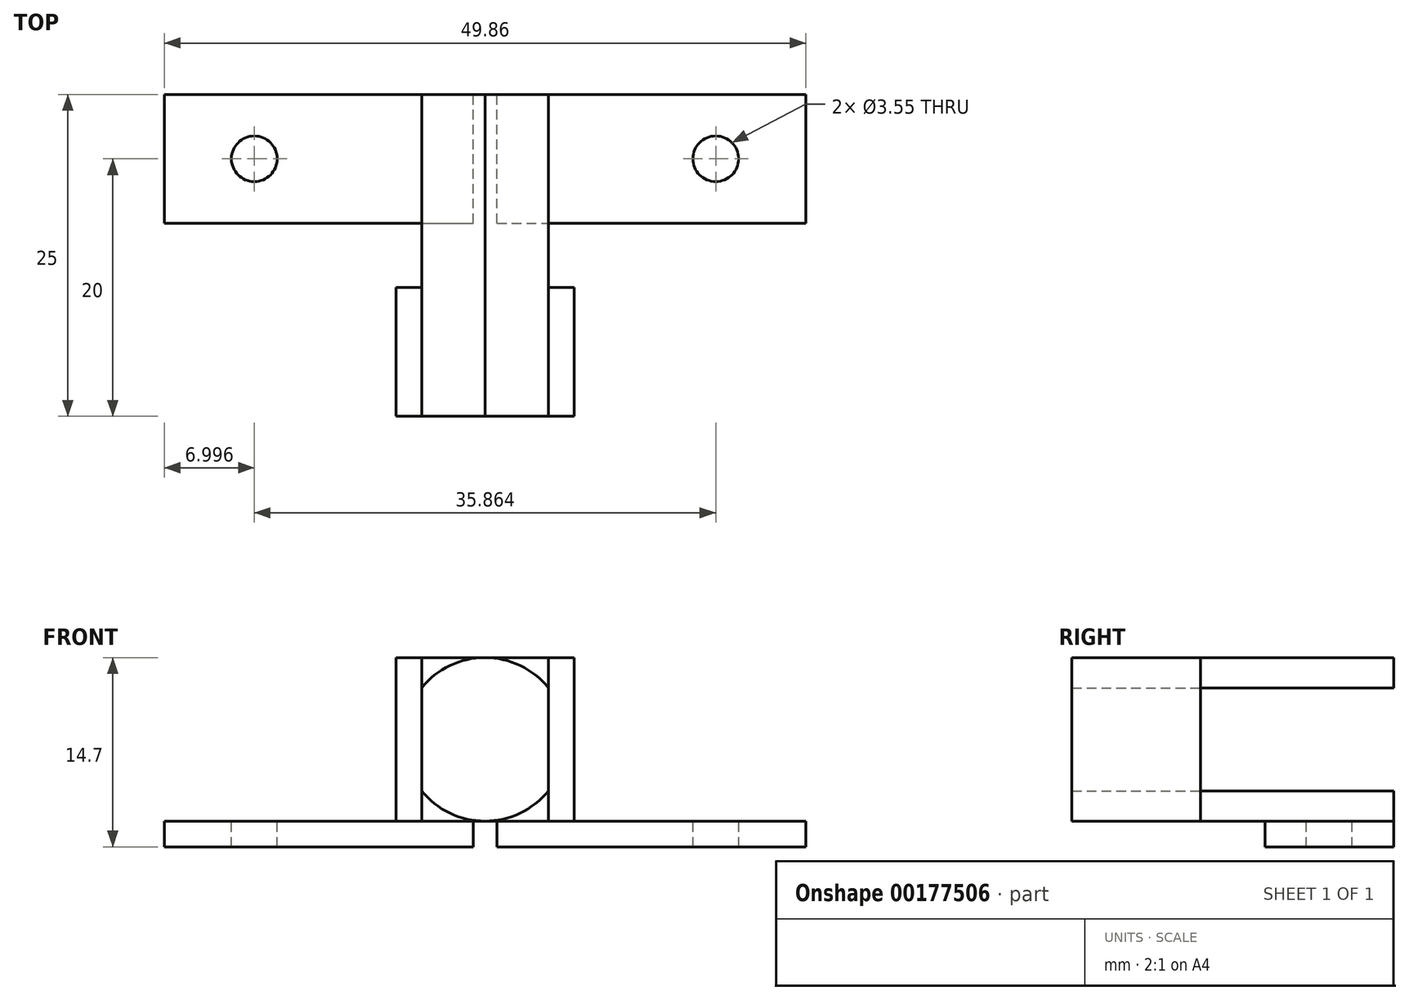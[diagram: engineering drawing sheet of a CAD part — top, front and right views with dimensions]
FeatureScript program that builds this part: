
annotation { "Feature Type Name" : "Feature", "Feature Type Description" : "" }
export const myFeature = defineFeature(function(context is Context, id is Id, definition is map)
    precondition{}
    {
        {
            var Q0;
            Q0=qCreatedBy(makeId("Front.planeOp"),FACE);
            var sketch = newSketch(context, id + "F0", { "sketchPlane" : qUnion([Q0])});
            skArc(sketch, "E0", {"start": v(-9.86, 0) * mm, "mid": v(-4.93, -2.35) * mm, "end": v(0, 0) * mm});
            skArc(sketch, "E1.MirrorCS", {"start": v(-9.86, 8) * mm, "mid": v(-4.93, 10.35) * mm, "end": v(0, 8) * mm});
            skLineSegment(sketch, "E2", {"start": v(-9.86, 8) * mm, "end": v(0, 8) * mm, "construction": true});
            skLineSegment(sketch, "E3", {"start": v(-9.86, 0) * mm, "end": v(0, 0) * mm, "construction": true});
            skLineSegment(sketch, "E4", {"start": v(0, 8) * mm, "end": v(0, 0) * mm, "construction": true});
            skCircle(sketch, "E5", {"center": v(-4.93, 4) * mm, "radius": 6.35 * mm, "construction": true});
            skPoint(sketch, "E6", {"position": v(0, 8) * mm});
            skPoint(sketch, "E7", {"position": v(1.42, 4) * mm});
            skLineSegment(sketch, "E8", {"start": v(-4.93, 4) * mm, "end": v(1.42, 4) * mm, "construction": true});
            skLineSegment(sketch, "E9", {"start": v(-9.86, 8) * mm, "end": v(-9.86, 10.35) * mm});
            skPoint(sketch, "E9.endSnap0", {"position": v(-4.93, 10.35) * mm});
            skLineSegment(sketch, "E10", {"start": v(-9.86, 10.35) * mm, "end": v(-4.93, 10.35) * mm});
            skLineSegment(sketch, "E11", {"start": v(0, 10.35) * mm, "end": v(0, 8) * mm});
            skLineSegment(sketch, "E12", {"start": v(0, 10.35) * mm, "end": v(-4.93, 10.35) * mm});
            skLineSegment(sketch, "E13", {"start": v(-4.93, -2.35) * mm, "end": v(-9.86, -2.35) * mm});
            skLineSegment(sketch, "E14", {"start": v(-9.86, -2.35) * mm, "end": v(-9.86, 0) * mm});
            skLineSegment(sketch, "E15", {"start": v(-4.93, -2.35) * mm, "end": v(0, -2.35) * mm});
            skLineSegment(sketch, "E16", {"start": v(0, -2.35) * mm, "end": v(0, 0) * mm});
            skSolve(sketch);
        }
        {
            var Q0;
            {var subQ0=sQuery(id+"F0.wireOp",EDGE,"E9");Q0=makeQuery(id+"F0.imprint","IMPRINT",FACE,{"disambiguationData":[TD([[makeQuery(id+"F0.imprint","IMPRINT",EDGE,{"derivedFrom":subQ0}),-1.0]])]});}
            var Q1;
            {var subQ0=sQuery(id+"F0.wireOp",EDGE,"E11");Q1=makeQuery(id+"F0.imprint","IMPRINT",FACE,{"disambiguationData":[TD([[makeQuery(id+"F0.imprint","IMPRINT",EDGE,{"derivedFrom":subQ0}),-1.0]])]});}
            var Q2;
            {var subQ2=sQuery(id+"F0.wireOp",EDGE,"E13");Q2=makeQuery(id+"F0.imprint","IMPRINT",FACE,{"disambiguationData":[TD([[makeQuery(id+"F0.imprint","IMPRINT",EDGE,{"derivedFrom":subQ2}),-1.0]])]});}
            var Q3;
            {var subQ2=sQuery(id+"F0.wireOp",EDGE,"E15");Q3=makeQuery(id+"F0.imprint","IMPRINT",FACE,{"disambiguationData":[TD([[makeQuery(id+"F0.imprint","IMPRINT",EDGE,{"derivedFrom":subQ2}),1.0]])]});}
            extrude(context, id + "F1", {"entities" : qUnion([Q0, Q1, Q2, Q3]), "depth" : 25 * mm});
        }
        {
            var Q0;
            Q0=makeQuery(id+"F1.opExtrude","SWEPT_FACE",FACE,{"disambiguationData":[OSD([sQuery(id+"F0.wireOp",EDGE,"E9")])]});
            var sketch = newSketch(context, id + "F2", { "sketchPlane" : qUnion([Q0])});
            skLineSegment(sketch, "E17", {"start": v(15, 10.35) * mm, "end": v(15, -2.35) * mm});
            skPoint(sketch, "E18", {"position": v(15, -2.35) * mm});
            skLineSegment(sketch, "E19", {"start": v(15, 10.35) * mm, "end": v(25, 10.35) * mm});
            skLineSegment(sketch, "E20", {"start": v(25, 10.35) * mm, "end": v(25, -2.35) * mm});
            skPoint(sketch, "E20.endSnap0", {"position": v(25, 9.17) * mm});
            skLineSegment(sketch, "E21", {"start": v(25, -2.35) * mm, "end": v(15, -2.35) * mm});
            skSolve(sketch);
        }
        {
            var Q0;
            {var subQ0=sQuery(id+"F2.wireOp",EDGE,"E21");Q0=makeQuery(id+"F2.imprint","IMPRINT",FACE,{"disambiguationData":[TD([[makeQuery(id+"F2.imprint","IMPRINT",EDGE,{"derivedFrom":subQ0}),-1.0]])]});}
            var Q1;
            {var subQ0=sQuery(id+"F2.wireOp",EDGE,"E19");Q1=makeQuery(id+"F2.imprint","IMPRINT",FACE,{"disambiguationData":[TD([[makeQuery(id+"F2.imprint","IMPRINT",EDGE,{"derivedFrom":subQ0}),1.0]])]});}
            extrude(context, id + "F3", {"entities" : qUnion([Q0, Q1]), "depth" : 2 * mm});
        }
        {
            var Q0;
            Q0=makeQuery(id+"F1.opExtrude","SWEPT_FACE",FACE,{"disambiguationData":[OSD([sQuery(id+"F0.wireOp",EDGE,"E11")])]});
            var sketch = newSketch(context, id + "F4", { "sketchPlane" : qUnion([Q0])});
            skLineSegment(sketch, "E22", {"start": v(-25, 10.35) * mm, "end": v(-25, -2.35) * mm});
            skLineSegment(sketch, "E23", {"start": v(-25, -2.35) * mm, "end": v(-15, -2.35) * mm});
            skLineSegment(sketch, "E24", {"start": v(-15, -2.35) * mm, "end": v(-15, 10.35) * mm});
            skLineSegment(sketch, "E25", {"start": v(-15, 10.35) * mm, "end": v(-25, 10.35) * mm});
            skSolve(sketch);
        }
        {
            var Q0;
            {var subQ4=sQuery(id+"F4.wireOp",EDGE,"E25");Q0=makeQuery(id+"F4.imprint","IMPRINT",FACE,{"disambiguationData":[TD([[makeQuery(id+"F4.imprint","IMPRINT",EDGE,{"derivedFrom":subQ4}),-1.0]])]});}
            var Q1;
            {var subQ3=sQuery(id+"F4.wireOp",EDGE,"E23");Q1=makeQuery(id+"F4.imprint","IMPRINT",FACE,{"disambiguationData":[TD([[makeQuery(id+"F4.imprint","IMPRINT",EDGE,{"derivedFrom":subQ3}),1.0]])]});}
            extrude(context, id + "F5", {"entities" : qUnion([Q0, Q1]), "depth" : 2 * mm});
        }
        {
            var Q0;
            Q0=makeQuery(id+"F1.opExtrude","SWEPT_FACE",FACE,{"disambiguationData":[OSD([sQuery(id+"F0.wireOp",EDGE,"E13")])]});
            var sketch = newSketch(context, id + "F6", { "sketchPlane" : qUnion([Q0])});
            skPoint(sketch, "E26", {"position": v(-9.86, 10) * mm});
            skPoint(sketch, "E27", {"position": v(-5.86, 10) * mm});
            skPoint(sketch, "E28", {"position": v(-5.86, 0) * mm});
            skPoint(sketch, "E29", {"position": v(-9.86, 0) * mm});
            skLineSegment(sketch, "E30", {"start": v(-5.86, 10) * mm, "end": v(-9.86, 10) * mm});
            skLineSegment(sketch, "E31", {"start": v(-5.86, 10) * mm, "end": v(-5.86, 0) * mm});
            skLineSegment(sketch, "E32", {"start": v(-9.86, 0) * mm, "end": v(-29.86, 0) * mm});
            skLineSegment(sketch, "E33", {"start": v(-29.86, 0) * mm, "end": v(-29.86, 10) * mm});
            skLineSegment(sketch, "E34", {"start": v(-29.86, 10) * mm, "end": v(-9.86, 10) * mm});
            skSolve(sketch);
        }
        {
            var Q0;
            {var subQ0=sQuery(id+"F6.wireOp",EDGE,"E32");Q0=makeQuery(id+"F6.imprint","IMPRINT",FACE,{"disambiguationData":[TD([[makeQuery(id+"F6.imprint","IMPRINT",EDGE,{"derivedFrom":subQ0}),-1.0]])]});}
            var Q1;
            {var subQ0=sQuery(id+"F6.wireOp",EDGE,"E30");Q1=makeQuery(id+"F6.imprint","IMPRINT",FACE,{"disambiguationData":[TD([[makeQuery(id+"F6.imprint","IMPRINT",EDGE,{"derivedFrom":subQ0}),1.0]])]});}
            extrude(context, id + "F7", {"entities" : qUnion([Q0, Q1]), "depth" : 2 * mm});
        }
        {
            var Q0;
            Q0=makeQuery(id+"F7.opExtrude","CAP_FACE",FACE,{"disambiguationData":[OSD([sQuery(id+"F0.wireOp",EDGE,"E13"),sQuery(id+"F6.wireOp",EDGE,"E30"),sQuery(id+"F6.wireOp",EDGE,"E31"),sQuery(id+"F6.wireOp",EDGE,"E32"),sQuery(id+"F6.wireOp",EDGE,"E33"),sQuery(id+"F6.wireOp",EDGE,"E34")])],"isStart":true});
            var sketch = newSketch(context, id + "F8", { "sketchPlane" : qUnion([Q0])});
            skLineSegment(sketch, "E35", {"start": v(-29.86, -5) * mm, "end": v(-22.86, -5) * mm});
            skCircle(sketch, "E36", {"center": v(-22.86, -5) * mm, "radius": 1.77 * mm});
            skSolve(sketch);
        }
        {
            var Q0;
            Q0=sQuery(id+"F8.wireOp",VERTEX,"E35.end");
            var Q1;
            Q1=makeQuery(id+"F7.opExtrude","SWEPT_BODY",BODY,{"disambiguationData":[OSD([sQuery(id+"F0.wireOp",EDGE,"E13"),sQuery(id+"F6.wireOp",EDGE,"E30"),sQuery(id+"F6.wireOp",EDGE,"E31"),sQuery(id+"F6.wireOp",EDGE,"E32"),sQuery(id+"F6.wireOp",EDGE,"E33"),sQuery(id+"F6.wireOp",EDGE,"E34")])]});
            hole(context, id + "F9", {"style" : HoleStyle.SIMPLE, "endStyle" : HoleEndStyle.THROUGH, "holeDiameter" : 3.55 * mm, "locations" : qUnion([Q0]), "scope" : qUnion([Q1]), "isTappedThrough" : true});
        }
        {
            var Q0;
            Q0=makeQuery(id+"F1.opExtrude","SWEPT_FACE",FACE,{"disambiguationData":[OSD([sQuery(id+"F0.wireOp",EDGE,"E15")])]});
            var sketch = newSketch(context, id + "F10", { "sketchPlane" : qUnion([Q0])});
            skPoint(sketch, "E37", {"position": v(0, 10) * mm});
            skLineSegment(sketch, "E38", {"start": v(0, 10) * mm, "end": v(-4, 10) * mm});
            skLineSegment(sketch, "E39", {"start": v(0, 0) * mm, "end": v(-4, 0) * mm});
            skLineSegment(sketch, "E40", {"start": v(-4, 10) * mm, "end": v(-4, 0) * mm});
            skLineSegment(sketch, "E41", {"start": v(0, 10) * mm, "end": v(20, 10) * mm});
            skLineSegment(sketch, "E42", {"start": v(0, 0) * mm, "end": v(20, 0) * mm});
            skLineSegment(sketch, "E43", {"start": v(20, 0) * mm, "end": v(20, 10) * mm});
            skSolve(sketch);
        }
        {
            var Q0;
            {var subQ0=sQuery(id+"F10.wireOp",EDGE,"E41");Q0=makeQuery(id+"F10.imprint","IMPRINT",FACE,{"disambiguationData":[TD([[makeQuery(id+"F10.imprint","IMPRINT",EDGE,{"derivedFrom":subQ0}),-1.0]])]});}
            var Q1;
            {var subQ0=sQuery(id+"F10.wireOp",EDGE,"E38");Q1=makeQuery(id+"F10.imprint","IMPRINT",FACE,{"disambiguationData":[TD([[makeQuery(id+"F10.imprint","IMPRINT",EDGE,{"derivedFrom":subQ0}),1.0]])]});}
            extrude(context, id + "F11", {"entities" : qUnion([Q0, Q1]), "operationType" : NewBodyOperationType.ADD, "depth" : 2 * mm});
        }
        {
            var Q0;
            Q0=makeQuery(id+"F11.opExtrude","CAP_FACE",FACE,{"disambiguationData":[OSD([sQuery(id+"F10.wireOp",EDGE,"E38"),sQuery(id+"F10.wireOp",EDGE,"E39"),sQuery(id+"F10.wireOp",EDGE,"E40"),sQuery(id+"F10.wireOp",EDGE,"E41"),sQuery(id+"F10.wireOp",EDGE,"E42"),sQuery(id+"F10.wireOp",EDGE,"E43")])],"isStart":true});
            var sketch = newSketch(context, id + "F12", { "sketchPlane" : qUnion([Q0])});
            skLineSegment(sketch, "E44", {"start": v(20, -5) * mm, "end": v(13, -5) * mm});
            skPoint(sketch, "E44.endSnap0", {"position": v(20, -5) * mm});
            skPoint(sketch, "E45", {"position": v(13, -5) * mm});
            skSolve(sketch);
        }
        {
            var Q0;
            Q0=sQuery(id+"F12.wireOp",VERTEX,"E45");
            var Q1;
            Q1=makeQuery(id+"F1.opExtrude","SWEPT_BODY",BODY,{"disambiguationData":[OSD([sQuery(id+"F0.wireOp",EDGE,"E0"),sQuery(id+"F0.wireOp",EDGE,"E15"),sQuery(id+"F0.wireOp",EDGE,"E16")])]});
            hole(context, id + "F13", {"style" : HoleStyle.SIMPLE, "endStyle" : HoleEndStyle.THROUGH, "holeDiameter" : 3.55 * mm, "locations" : qUnion([Q0]), "scope" : qUnion([Q1]), "isTappedThrough" : true});
        }
    });
